# Revit family: Condensing-Solar-Water-Heater-Gas_AO_Smith-SGE_40_PN
name_source: partatom
category: Mechanical Equipment
revit_build: Autodesk Revit 2014 (Build: 20140709_2115(x64)
units: mm (PartAtom-declared; Revit-internal decimal feet)

## types (1)
- Condensing-Solar-Water-Heater-Gas_AO_Smith-SGE_40_PN
    (Additional Control) Frequency = 50 Hz
    (Additional Control) Phase = 1
    (Additional Control) Power Consumption (nominal) = 700 W
    (Additional Control) Voltage = 230 V
    1e Maintenance (check-up) = 3 maanden na installatie
    2nd Maintenance (general maintenance) = 12 maanden na installatie
    APS Pressure < = 115.0 Pa
    Assembly Code = D3010
    BIM Content Developer = CAD & Company
    CE-PIN = 0063BU3889
    Co2 Emissions (tol. +/- 1.0) vol% = 12.0/10.0
    Cold Water Connection R = 1 1/2"
    Condens Discharge Connection = 40 mm  [stored 0.131234 ft]
    Default Setpoint = 65 °C
    Description = HR-Condenserende Gas-Zonneboiler
    Destination / Country = Nederland
    Diameter = 705 mm  [stored 2.31299 ft]
    Drain Valve Connection Rp = 1"
    Draw-off Capacity @ ΔT = 28°C after 120 min. = 2800.0 L
    Draw-off Capacity @ ΔT = 28°C after 30 min. = 810.0 L
    Draw-off Capacity @ ΔT = 28°C after 60 min. = 1500.0 L
    Draw-off Capacity @ ΔT = 28°C after 90 min. = 2200.0 L
    Draw-off Capacity @ ΔT = 44°C after 120 min. = 1800.0 L
    Draw-off Capacity @ ΔT = 44°C after 30 min. = 470.0 L
    Draw-off Capacity @ ΔT = 44°C after 60 min. = 890.0 L
    Draw-off Capacity @ ΔT = 44°C after 90 min. = 1400.0 L
    Draw-off Capacity @ ΔT = 50°C after 120 min. = 1500.0 L
    Draw-off Capacity @ ΔT = 50°C after 30 min. = 400.0 L
    Draw-off Capacity @ ΔT = 50°C after 60 min. = 760.0 L
    Draw-off Capacity @ ΔT = 50°C after 90 min. = 1200.0 L
    Draw-off Capacity @ ΔT = 55°C after 120 min. = 1400.0 L
    Draw-off Capacity @ ΔT = 55°C after 30 min. = 340.0 L
    Draw-off Capacity @ ΔT = 55°C after 60 min. = 680.0 L
    Draw-off Capacity @ ΔT = 55°C after 90 min. = 1100.0 L
    Draw-off Capacity @ ΔT = 70°C after 120 min. = 0.0 L
    Draw-off Capacity @ ΔT = 70°C after 30 min. = 0.0 L
    Draw-off Capacity @ ΔT = 70°C after 60 min. = 0.0 L
    Draw-off Capacity @ ΔT = 70°C after 90 min. = 0.0 L
    Empty Weight = 245 kg
    Energy Efficiency Rating (Hi, acc NEN-EN 89-1999) = 107
    Energy Efficiency Rating (Hs, acc NEN-EN 89-1999) = 96
    Flue Diameter - concentric system = 100/150 mm/mm
    Flue Diameter - parallel system = 100 mm  [stored 0.328084 ft]
    Flue Diameter - water heater = 100/150 mm/mm
    Frequency = 50 Hz
    Gas Category = II2EK3B/P
    Gas Connection R = 3/4"
    Gas Flow Rate - Mass kg/h = 3.60/3.10
    Gas Flow Rate - Volume ltr/hr = 0
    Heating Up Time @ ΔT = 28°C = 9
    Heating Up Time @ ΔT = 44°C = 15
    Heating Up Time @ ΔT = 50°C = 17
    Heating Up Time @ ΔT = 55°C = 18
    Height = 2065 mm  [stored 6.77493 ft]
    Height Air Inlet = 1995 mm  [stored 6.54528 ft]
    Height Cold water Intlet = 185 mm  [stored 0.606955 ft]
    Height Flue Outlet = 1995 mm  [stored 6.54528 ft]
    Height Gas Connection = 1960 mm  [stored 6.43045 ft]
    Height Warm Water Outlet = 2055 mm  [stored 6.74213 ft]
    Hot / Warm Water Connection R = 1 1/2"
    Installation Type = B23/C13/C33/C43/C53/C63
    Insulation Thickness = 50 mm  [stored 0.164042 ft]
    Length = 925 mm  [stored 3.03478 ft]
    Maintenance Interval = 12 maanden
    Manufacturer = A.O. Smith Water Products Company b.v.
    Manufacturer Number = E 7110
    Max. Flue Gas Outlet Temperature = 50 °C
    Max. Operating Pressure = 800000.0 Pa
    Max. Setpoint = 80 °C
    Min. Setpoint = 40 °C
    Model = SNE 40 PN
    NOx Emissions (air free, 0% O2) ppm = 66.0/20.0
    NOx Emissions mg/kWh = 117.0/35.0
    Noice-level dB (A) = 45
    Nominal Heat Input (Gross) = 49900.0/43500.0
    Nominal Heat Input (Net) = 46000.0/40000.0
    Nominal Output = 49200.0/42800.0
    Operating Weight = 615 kg
    Packaging Height = 2100 mm
    Packaging Length = 945 mm  [stored 3.10039 ft]
    Packaging Width = 870 mm  [stored 2.85433 ft]
    Phase = 1
    Power Consumption (nominal) = 60 W
    Product Documentation Link = https://www.aosmithinternational.com
    Product Instruction Link = https://www.aosmithinternational.com
    Recovery Rate @ ΔT = 28°C = 1400.0 L/s
    Recovery Rate @ ΔT = 44°C = 840.0 L/s
    Recovery Rate @ ΔT = 50°C = 740.0 L/s
    Recovery Rate @ ΔT = 55°C = 670.0 L/s
    Recovery Rate @ ΔT = 70°C = 0.0 L/s
    Seasonal Energy Efficiency Rating = 96
    Serial Number = 8717449195137
    Stand-by Loss = 0 W
    Stand-by Loss - daily (24h) = 0 W
    Standard Set For = G30/G31
    Storage Capacity = 370.0 L
    Supply Pressure min/max = 3000 - 5000 Pa
    T&P Connection Rp = 1"
    Transport Weight = 256 kg
    Type of Packaging = Plastic Krimpverpakking, Karton en Hout
    URL = www.aosmith.nl
    Voltage = 230 V
    Warranty on parts = 12 maanden
    Warranty on tank = 36 maanden
    Width = 850 mm  [stored 2.78871 ft]

note: [stored X ft] marks values corroborated as IEEE doubles in the binary element streams (Revit-internal decimal feet)

## geometry (parser evidence)
native form markers: Blend x13, Sweep x53
no freeform markers — native parametric forms only
